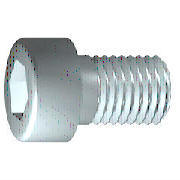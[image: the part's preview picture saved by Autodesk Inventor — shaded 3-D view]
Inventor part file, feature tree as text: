
AUTODESK INVENTOR PART (.ipt)
format: ipt  version: 2018 (Build 220112000, 112)  size: 188,928 bytes
history: native  units: mm (DEFAULTED — no unit token found)
features: sketch x2, extrude x1, plane x1, fillet x1
ambient origin geometry x7: Origin, YZ Plane, XY Plane, X Axis, Y Axis, Z Axis, Center Point
bodies: Solid1 (feature_tree), Body (feature_tree)
feature tree (5):
  extrude  "Slot"  Depth=5.0mm
  plane  "Work Plane1"
  fillet  "Fillet2"  Radius=5.0mm
  sketch  "Sketch1"  dims[d1=23.51848mm d2=0.49086mm d3=5.0mm]
  sketch  "Sketch2"  dims[d4=2.5mm d5=60.0deg d6=5.0mm d7=5.0mm d8=4.618802mm d9=8.5mm d10=90.0deg d11=10.0mm d12=0.0mm d13=23.51848mm d14=0.0mm d15=0.49076mm d16=0.49076mm d17=0.5mm d19=0.0mm d26=25.0mm d27=45.0deg d28=0.0mm d29=0.0mm d30=0.1mm]
